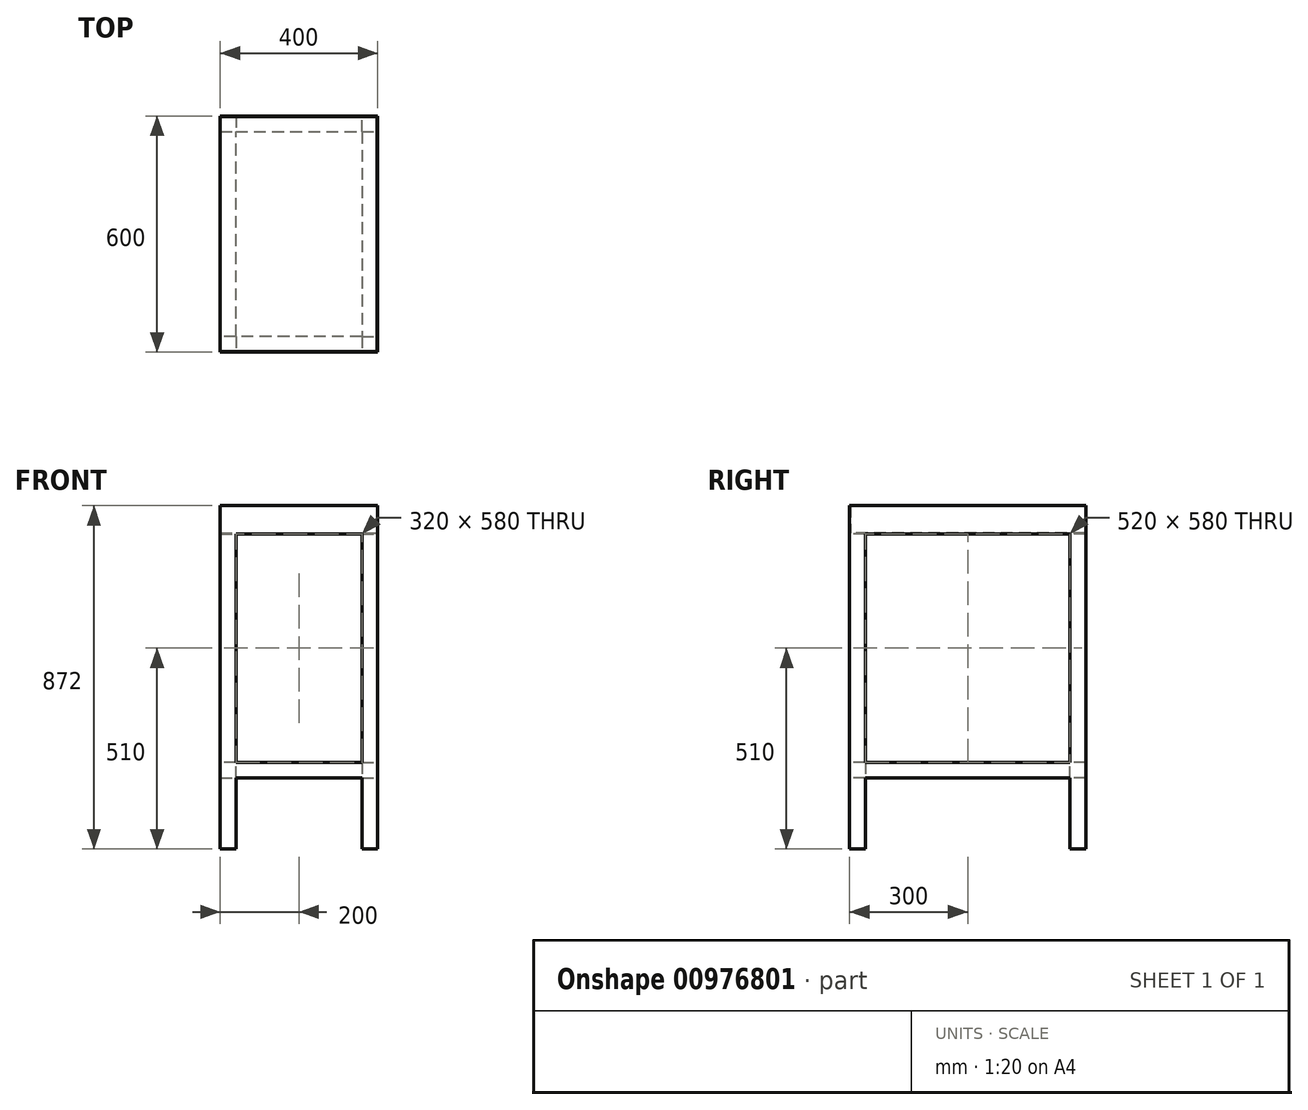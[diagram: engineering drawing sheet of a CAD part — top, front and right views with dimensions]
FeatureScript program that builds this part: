
annotation { "Feature Type Name" : "Feature", "Feature Type Description" : "" }
export const myFeature = defineFeature(function(context is Context, id is Id, definition is map)
    precondition{}
    {
        {
            var Q0;
            Q0=qCreatedBy(makeId("Top.planeOp"),FACE);
            var sketch = newSketch(context, id + "F0", { "sketchPlane" : qUnion([Q0])});
            skLineSegment(sketch, "E0.bottom", {"start": v(-200, 300) * mm, "end": v(-160, 300) * mm});
            skLineSegment(sketch, "E0.top", {"start": v(-200, 260) * mm, "end": v(-160, 260) * mm});
            skLineSegment(sketch, "E0.left", {"start": v(-200, 300) * mm, "end": v(-200, 260) * mm});
            skLineSegment(sketch, "E0.right", {"start": v(-160, 300) * mm, "end": v(-160, 260) * mm});
            skLineSegment(sketch, "E1.bottom", {"start": v(-200, -260) * mm, "end": v(-160, -260) * mm});
            skLineSegment(sketch, "E1.top", {"start": v(-200, -300) * mm, "end": v(-160, -300) * mm});
            skLineSegment(sketch, "E1.left", {"start": v(-200, -260) * mm, "end": v(-200, -300) * mm});
            skLineSegment(sketch, "E1.right", {"start": v(-160, -260) * mm, "end": v(-160, -300) * mm});
            skLineSegment(sketch, "E2.bottom", {"start": v(160, 260) * mm, "end": v(200, 260) * mm});
            skLineSegment(sketch, "E2.top", {"start": v(160, 300) * mm, "end": v(200, 300) * mm});
            skLineSegment(sketch, "E2.left", {"start": v(160, 260) * mm, "end": v(160, 300) * mm});
            skLineSegment(sketch, "E2.right", {"start": v(200, 260) * mm, "end": v(200, 300) * mm});
            skLineSegment(sketch, "E3.bottom", {"start": v(160, -260) * mm, "end": v(200, -260) * mm});
            skLineSegment(sketch, "E3.top", {"start": v(160, -300) * mm, "end": v(200, -300) * mm});
            skLineSegment(sketch, "E3.left", {"start": v(160, -260) * mm, "end": v(160, -300) * mm});
            skLineSegment(sketch, "E3.right", {"start": v(200, -260) * mm, "end": v(200, -300) * mm});
            skLineSegment(sketch, "E4", {"start": v(-344.67, 0) * mm, "end": v(281.73, 0) * mm, "construction": true});
            skLineSegment(sketch, "E5", {"start": v(0, 256.35) * mm, "end": v(0, -215.74) * mm, "construction": true});
            skSolve(sketch);
        }
        {
            var Q0;
            Q0 = qSketchRegion(id + "F0", true);
            extrude(context, id + "F1", {"entities" : qUnion([Q0]), "depth" : 800 * mm, "offsetDistance" : 25.4 * mm});
        }
        {
            var Q0;
            Q0=makeQuery(id+"F1.opExtrude","CAP_FACE",FACE,{"disambiguationData":[OSD([sQuery(id+"F0.wireOp",EDGE,"E0.bottom"),sQuery(id+"F0.wireOp",EDGE,"E0.top"),sQuery(id+"F0.wireOp",EDGE,"E0.left"),sQuery(id+"F0.wireOp",EDGE,"E0.right")])],"isStart":false});
            var sketch = newSketch(context, id + "F2", { "sketchPlane" : qUnion([Q0])});
            skLineSegment(sketch, "E6.bottom", {"start": v(-200, 300) * mm, "end": v(200, 300) * mm});
            skLineSegment(sketch, "E6.top", {"start": v(-200, -300) * mm, "end": v(200, -300) * mm});
            skLineSegment(sketch, "E6.left", {"start": v(-200, 300) * mm, "end": v(-200, -300) * mm});
            skLineSegment(sketch, "E6.right", {"start": v(200, 300) * mm, "end": v(200, -300) * mm});
            skSolve(sketch);
        }
        {
            var Q0;
            Q0 = qSketchRegion(id + "F2", true);
            extrude(context, id + "F3", {"entities" : qUnion([Q0]), "operationType" : NewBodyOperationType.ADD, "depth" : 2 * mm, "offsetDistance" : 25.4 * mm});
        }
        {
            var Q0;
            Q0=makeQuery(id+"F3.opExtrude","CAP_FACE",FACE,{"disambiguationData":[OSD([sQuery(id+"F2.wireOp",EDGE,"E6.bottom"),sQuery(id+"F2.wireOp",EDGE,"E6.top"),sQuery(id+"F2.wireOp",EDGE,"E6.left"),sQuery(id+"F2.wireOp",EDGE,"E6.right")])],"isStart":false});
            var sketch = newSketch(context, id + "F4", { "sketchPlane" : qUnion([Q0])});
            skLineSegment(sketch, "E7", {"start": v(-200, 300) * mm, "end": v(200, 300) * mm});
            skLineSegment(sketch, "E8", {"start": v(200, 300) * mm, "end": v(200, -300) * mm});
            skLineSegment(sketch, "E9", {"start": v(200, -300) * mm, "end": v(-200, -300) * mm});
            skLineSegment(sketch, "E10.0", {"start": v(198, -298) * mm, "end": v(-200, -298) * mm});
            skLineSegment(sketch, "E10.1", {"start": v(198, 298) * mm, "end": v(198, -298) * mm});
            skLineSegment(sketch, "E10.2", {"start": v(-200, 298) * mm, "end": v(198, 298) * mm});
            skLineSegment(sketch, "E11", {"start": v(-200, 300) * mm, "end": v(-200, 298) * mm});
            skLineSegment(sketch, "E12", {"start": v(-200, -300) * mm, "end": v(-200, -298) * mm});
            skSolve(sketch);
        }
        {
            var Q0;
            Q0 = qSketchRegion(id + "F4", true);
            extrude(context, id + "F5", {"entities" : qUnion([Q0]), "operationType" : NewBodyOperationType.ADD, "depth" : 70 * mm, "offsetDistance" : 25.4 * mm});
        }
        {
            var Q0;
            Q0=makeQuery(id+"F1.opExtrude","SWEPT_FACE",FACE,{"disambiguationData":[OSD([sQuery(id+"F0.wireOp",EDGE,"E0.top")])]});
            var sketch = newSketch(context, id + "F6", { "sketchPlane" : qUnion([Q0])});
            skLineSegment(sketch, "E13.bottom", {"start": v(-200, 220) * mm, "end": v(-160, 220) * mm});
            skLineSegment(sketch, "E13.top", {"start": v(-200, 180) * mm, "end": v(-160, 180) * mm});
            skLineSegment(sketch, "E13.left", {"start": v(-200, 220) * mm, "end": v(-200, 180) * mm});
            skLineSegment(sketch, "E13.right", {"start": v(-160, 220) * mm, "end": v(-160, 180) * mm});
            skSolve(sketch);
        }
        {
            var Q0;
            Q0 = qSketchRegion(id + "F6", true);
            extrude(context, id + "F7", {"entities" : qUnion([Q0]), "operationType" : NewBodyOperationType.ADD, "endBound" : BoundingType.UP_TO_NEXT, "depth" : 25.4 * mm, "offsetDistance" : 25.4 * mm});
        }
        {
            var Q0;
            Q0=makeQuery(id+"F1.opExtrude","SWEPT_FACE",FACE,{"disambiguationData":[OSD([sQuery(id+"F0.wireOp",EDGE,"E1.right")])]});
            var sketch = newSketch(context, id + "F8", { "sketchPlane" : qUnion([Q0])});
            skLineSegment(sketch, "E14.bottom", {"start": v(-260, 220) * mm, "end": v(-300, 220) * mm});
            skLineSegment(sketch, "E14.top", {"start": v(-260, 180) * mm, "end": v(-300, 180) * mm});
            skLineSegment(sketch, "E14.left", {"start": v(-260, 220) * mm, "end": v(-260, 180) * mm});
            skLineSegment(sketch, "E14.right", {"start": v(-300, 220) * mm, "end": v(-300, 180) * mm});
            skSolve(sketch);
        }
        {
            var Q0;
            Q0 = qSketchRegion(id + "F8", true);
            extrude(context, id + "F9", {"entities" : qUnion([Q0]), "operationType" : NewBodyOperationType.ADD, "endBound" : BoundingType.UP_TO_NEXT, "depth" : 25.4 * mm, "offsetDistance" : 25.4 * mm});
        }
        {
            var Q0;
            Q0=makeQuery(id+"F1.opExtrude","SWEPT_FACE",FACE,{"disambiguationData":[OSD([sQuery(id+"F0.wireOp",EDGE,"E3.bottom")])]});
            var sketch = newSketch(context, id + "F10", { "sketchPlane" : qUnion([Q0])});
            skLineSegment(sketch, "E15.bottom", {"start": v(-160, 220) * mm, "end": v(-200, 220) * mm});
            skLineSegment(sketch, "E15.top", {"start": v(-160, 180) * mm, "end": v(-200, 180) * mm});
            skLineSegment(sketch, "E15.left", {"start": v(-160, 220) * mm, "end": v(-160, 180) * mm});
            skLineSegment(sketch, "E15.right", {"start": v(-200, 220) * mm, "end": v(-200, 180) * mm});
            skSolve(sketch);
        }
        {
            var Q0;
            Q0 = qSketchRegion(id + "F10", true);
            extrude(context, id + "F11", {"entities" : qUnion([Q0]), "operationType" : NewBodyOperationType.ADD, "endBound" : BoundingType.UP_TO_NEXT, "depth" : 25.4 * mm, "offsetDistance" : 25.4 * mm});
        }
        {
            var Q0;
            Q0=makeQuery(id+"F1.opExtrude","SWEPT_FACE",FACE,{"disambiguationData":[OSD([sQuery(id+"F0.wireOp",EDGE,"E2.left")])]});
            var sketch = newSketch(context, id + "F12", { "sketchPlane" : qUnion([Q0])});
            skLineSegment(sketch, "E16.bottom", {"start": v(-260, 220) * mm, "end": v(-300, 220) * mm});
            skLineSegment(sketch, "E16.top", {"start": v(-260, 180) * mm, "end": v(-300, 180) * mm});
            skLineSegment(sketch, "E16.left", {"start": v(-260, 220) * mm, "end": v(-260, 180) * mm});
            skLineSegment(sketch, "E16.right", {"start": v(-300, 220) * mm, "end": v(-300, 180) * mm});
            skSolve(sketch);
        }
        {
            var Q0;
            Q0 = qSketchRegion(id + "F12", true);
            extrude(context, id + "F13", {"entities" : qUnion([Q0]), "operationType" : NewBodyOperationType.ADD, "endBound" : BoundingType.UP_TO_NEXT, "depth" : 25.4 * mm, "offsetDistance" : 25.4 * mm});
        }
    });
